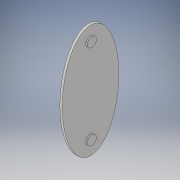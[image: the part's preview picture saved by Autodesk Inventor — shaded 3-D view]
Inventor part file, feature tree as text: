
AUTODESK INVENTOR PART (.ipt)
format: ipt  version: 2017 (Build 210142000, 142)  size: 109,056 bytes
history: native  units: in
note: dims shown in document units (in); Inventor stores cm internally (conversion verified against a paired STEP export)
features: extrude x2, sketch x2
ambient origin geometry x8: Origin, YZ Plane, XZ Plane, XY Plane, X Axis, Y Axis, Z Axis, Center Point
bodies: Solid1 (feature_tree)
feature tree (4):
  extrude  "Extrusion1"  Depth=3.0in
  extrude  "Extrusion2"  Depth=0.0625in
  sketch  "Sketch1"  dims[d0=1.5in d1=3.0in]
  sketch  "Sketch2"  dims[d2=0.125in d3=0.0in d4=2.25in d5=2.25in d6=0.501in d7=0.501in d8=0.0625in d9=0.0in]
